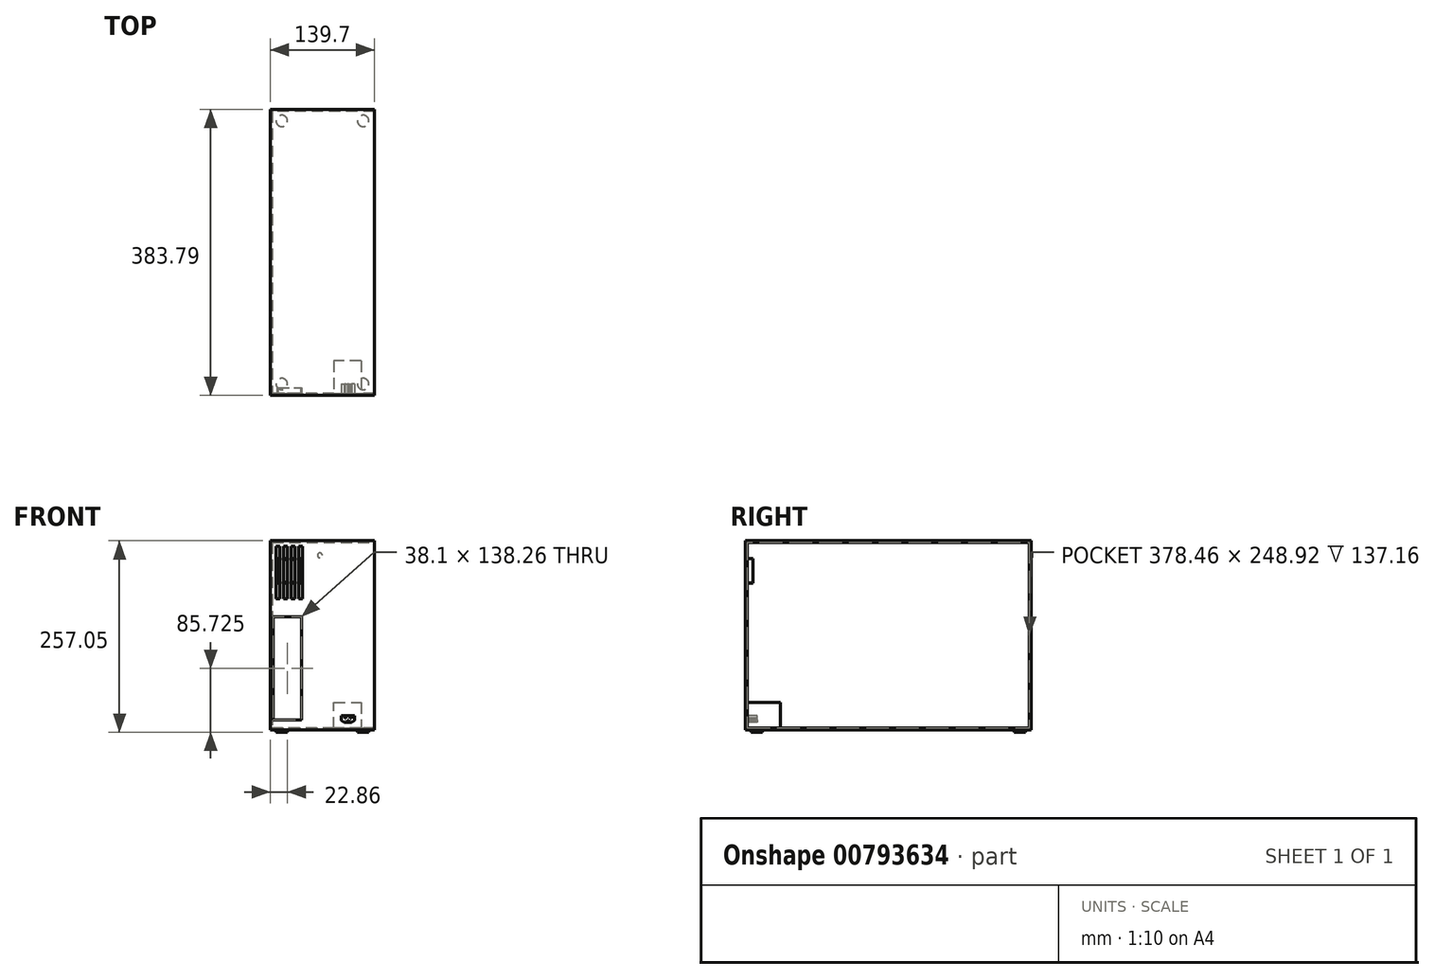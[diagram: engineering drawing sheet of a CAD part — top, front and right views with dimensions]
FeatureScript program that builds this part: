
annotation { "Feature Type Name" : "Feature", "Feature Type Description" : "" }
export const myFeature = defineFeature(function(context is Context, id is Id, definition is map)
    precondition{}
    {
        {
            var Q0;
            Q0=qCreatedBy(makeId("Top.planeOp"),FACE);
            var sketch = newSketch(context, id + "F0", { "sketchPlane" : qUnion([Q0])});
            skLineSegment(sketch, "E0", {"start": v(0, 0) * mm, "end": v(0, 381) * mm});
            skLineSegment(sketch, "E1", {"start": v(0, 381) * mm, "end": v(139.7, 381) * mm});
            skLineSegment(sketch, "E2", {"start": v(139.7, 381) * mm, "end": v(139.7, 0) * mm});
            skLineSegment(sketch, "E3", {"start": v(139.7, 0) * mm, "end": v(0, 0) * mm});
            skSolve(sketch);
        }
        {
            var Q0;
            Q0 = qSketchRegion(id + "F0", true);
            extrude(context, id + "F1", {"entities" : qUnion([Q0]), "depth" : 2.54 * mm, "offsetDistance" : 25.4 * mm});
        }
        {
            var Q0;
            Q0=qCreatedBy(makeId("Front.planeOp"),FACE);
            var sketch = newSketch(context, id + "F2", { "sketchPlane" : qUnion([Q0])});
            skLineSegment(sketch, "E4", {"start": v(0, 0) * mm, "end": v(0, 254) * mm});
            skLineSegment(sketch, "E5", {"start": v(0, 254) * mm, "end": v(139.7, 254) * mm});
            skLineSegment(sketch, "E6", {"start": v(139.7, 254) * mm, "end": v(139.7, 0) * mm});
            skLineSegment(sketch, "E7", {"start": v(139.7, 0) * mm, "end": v(0, 0) * mm});
            skSolve(sketch);
        }
        {
            var Q0;
            Q0 = qSketchRegion(id + "F2", true);
            extrude(context, id + "F3", {"entities" : qUnion([Q0]), "operationType" : NewBodyOperationType.ADD, "depth" : 2.54 * mm, "offsetDistance" : 25.4 * mm});
        }
        {
            var Q0;
            Q0=qCreatedBy(makeId("Right.planeOp"),FACE);
            var sketch = newSketch(context, id + "F4", { "sketchPlane" : qUnion([Q0])});
            skLineSegment(sketch, "E8", {"start": v(0, 0) * mm, "end": v(381, 0) * mm});
            skLineSegment(sketch, "E9", {"start": v(381, 0) * mm, "end": v(381, 254) * mm});
            skLineSegment(sketch, "E10", {"start": v(381, 254) * mm, "end": v(0, 254) * mm});
            skLineSegment(sketch, "E11", {"start": v(0, 254) * mm, "end": v(0, 0) * mm});
            skSolve(sketch);
        }
        {
            var Q0;
            Q0 = qSketchRegion(id + "F4", true);
            extrude(context, id + "F5", {"entities" : qUnion([Q0]), "operationType" : NewBodyOperationType.ADD, "depth" : 2.54 * mm, "offsetDistance" : 25.4 * mm});
        }
        {
            var Q0;
            Q0=qCreatedBy(makeId("Front.planeOp"),FACE);
            cPlane(context, id + "F6", {"entities" : qUnion([Q0]), "cplaneType" : CPlaneType.OFFSET, "offset" : 381 * mm, "oppositeDirection" : true, "width" : 152.4 * mm, "height" : 152.4 * mm});
        }
        {
            var Q0;
            Q0=qCreatedBy(id+"F6.planeOp",FACE);
            var sketch = newSketch(context, id + "F7", { "sketchPlane" : qUnion([Q0])});
            skLineSegment(sketch, "E12", {"start": v(0, 0) * mm, "end": v(0, 254) * mm});
            skLineSegment(sketch, "E13", {"start": v(0, 254) * mm, "end": v(139.7, 254) * mm});
            skLineSegment(sketch, "E14", {"start": v(139.7, 254) * mm, "end": v(139.7, 0) * mm});
            skLineSegment(sketch, "E15", {"start": v(139.7, 0) * mm, "end": v(0, 0) * mm});
            skSolve(sketch);
        }
        {
            var Q0;
            Q0 = qSketchRegion(id + "F7", true);
            extrude(context, id + "F8", {"entities" : qUnion([Q0]), "operationType" : NewBodyOperationType.ADD, "depth" : 2.54 * mm, "offsetDistance" : 25.4 * mm});
        }
        {
            var Q0;
            Q0=qCreatedBy(makeId("Top.planeOp"),FACE);
            cPlane(context, id + "F9", {"entities" : qUnion([Q0]), "cplaneType" : CPlaneType.OFFSET, "offset" : 254 * mm, "width" : 152.4 * mm, "height" : 152.4 * mm});
        }
        {
            var Q0;
            Q0=qCreatedBy(id+"F9.planeOp",FACE);
            var sketch = newSketch(context, id + "F10", { "sketchPlane" : qUnion([Q0])});
            skLineSegment(sketch, "E16", {"start": v(0, 0) * mm, "end": v(139.7, 0) * mm});
            skLineSegment(sketch, "E17", {"start": v(139.7, 0) * mm, "end": v(139.7, 381) * mm});
            skLineSegment(sketch, "E18", {"start": v(139.7, 381) * mm, "end": v(0, 381) * mm});
            skLineSegment(sketch, "E19", {"start": v(0, 381) * mm, "end": v(0, 0) * mm});
            skSolve(sketch);
        }
        {
            var Q0;
            Q0 = qSketchRegion(id + "F10", true);
            extrude(context, id + "F11", {"entities" : qUnion([Q0]), "operationType" : NewBodyOperationType.ADD, "oppositeDirection" : true, "depth" : 2.54 * mm, "offsetDistance" : 25.4 * mm});
        }
        {
            var Q0;
            Q0=makeQuery(id+"F3.opExtrude","CAP_FACE",FACE,{"disambiguationData":[OSD([sQuery(id+"F2.wireOp",EDGE,"E4"),sQuery(id+"F2.wireOp",EDGE,"E5"),sQuery(id+"F2.wireOp",EDGE,"E6"),sQuery(id+"F2.wireOp",EDGE,"E7")])],"isStart":false});
            var sketch = newSketch(context, id + "F12", { "sketchPlane" : qUnion([Q0])});
            skLineSegment(sketch, "E20", {"start": v(7.62, 175.93) * mm, "end": v(7.62, 246.38) * mm});
            skLineSegment(sketch, "E21", {"start": v(7.62, 246.38) * mm, "end": v(12.7, 246.38) * mm});
            skLineSegment(sketch, "E22", {"start": v(12.7, 246.38) * mm, "end": v(12.7, 175.93) * mm});
            skLineSegment(sketch, "E23", {"start": v(12.7, 7.62) * mm, "end": v(7.62, 7.62) * mm});
            skLineSegment(sketch, "E24", {"start": v(17.78, 246.38) * mm, "end": v(17.78, 175.93) * mm});
            skLineSegment(sketch, "E25", {"start": v(17.78, 7.62) * mm, "end": v(22.86, 7.62) * mm});
            skLineSegment(sketch, "E26", {"start": v(22.86, 175.93) * mm, "end": v(22.86, 246.38) * mm});
            skLineSegment(sketch, "E27", {"start": v(22.86, 246.38) * mm, "end": v(17.78, 246.38) * mm});
            skLineSegment(sketch, "E28", {"start": v(27.94, 246.38) * mm, "end": v(27.94, 175.93) * mm});
            skLineSegment(sketch, "E29", {"start": v(27.94, 7.62) * mm, "end": v(33.02, 7.62) * mm});
            skLineSegment(sketch, "E30", {"start": v(33.02, 175.93) * mm, "end": v(33.02, 246.38) * mm});
            skLineSegment(sketch, "E31", {"start": v(33.02, 246.38) * mm, "end": v(27.94, 246.38) * mm});
            skLineSegment(sketch, "E32", {"start": v(38.1, 246.38) * mm, "end": v(38.1, 175.93) * mm});
            skLineSegment(sketch, "E33", {"start": v(38.1, 7.62) * mm, "end": v(43.18, 7.62) * mm});
            skLineSegment(sketch, "E34", {"start": v(43.18, 175.93) * mm, "end": v(43.18, 246.38) * mm});
            skLineSegment(sketch, "E35", {"start": v(43.18, 246.38) * mm, "end": v(38.1, 246.38) * mm});
            skLineSegment(sketch, "E36", {"start": v(7.62, 175.93) * mm, "end": v(12.7, 175.93) * mm});
            skLineSegment(sketch, "E37.trimOffspring", {"start": v(17.78, 175.93) * mm, "end": v(22.86, 175.93) * mm});
            skLineSegment(sketch, "E38.trimOffspring", {"start": v(27.94, 175.93) * mm, "end": v(33.02, 175.93) * mm});
            skLineSegment(sketch, "E39.trimOffspring", {"start": v(38.1, 175.93) * mm, "end": v(43.18, 175.93) * mm});
            skSolve(sketch);
        }
        {
            var Q0;
            Q0=makeQuery(id+"F12.imprint","IMPRINT",FACE,{"disambiguationData":[TD([[makeQuery(id+"F12.imprint","IMPRINT",EDGE,{"derivedFrom":sQuery(id+"F12.wireOp",EDGE,"E32")}),1.0]])]});
            var Q1;
            Q1=makeQuery(id+"F12.imprint","IMPRINT",FACE,{"disambiguationData":[TD([[makeQuery(id+"F12.imprint","IMPRINT",EDGE,{"derivedFrom":sQuery(id+"F12.wireOp",EDGE,"E28")}),1.0]])]});
            var Q2;
            Q2=makeQuery(id+"F12.imprint","IMPRINT",FACE,{"disambiguationData":[TD([[makeQuery(id+"F12.imprint","IMPRINT",EDGE,{"derivedFrom":sQuery(id+"F12.wireOp",EDGE,"E24")}),1.0]])]});
            var Q3;
            Q3=makeQuery(id+"F12.imprint","IMPRINT",FACE,{"disambiguationData":[TD([[makeQuery(id+"F12.imprint","IMPRINT",EDGE,{"derivedFrom":sQuery(id+"F12.wireOp",EDGE,"E20")}),-1.0]])]});
            extrude(context, id + "F13", {"entities" : qUnion([Q0, Q1, Q2, Q3]), "operationType" : NewBodyOperationType.REMOVE, "oppositeDirection" : true, "depth" : 2.54 * mm, "offsetDistance" : 25.4 * mm});
        }
        {
            var Q0;
            Q0=qCreatedBy(makeId("Front.planeOp"),FACE);
            var sketch = newSketch(context, id + "F14", { "sketchPlane" : qUnion([Q0])});
            skLineSegment(sketch, "E40", {"start": v(0, 0) * mm, "end": v(0, 238.76) * mm});
            skLineSegment(sketch, "E41", {"start": v(40.69, 228.6) * mm, "end": v(40.69, 198.12) * mm});
            skLineSegment(sketch, "E42", {"start": v(10.21, 198.12) * mm, "end": v(10.21, 228.6) * mm});
            skLineSegment(sketch, "E43", {"start": v(40.69, 198.12) * mm, "end": v(40.69, 228.6) * mm});
            skLineSegment(sketch, "E44", {"start": v(40.69, 228.6) * mm, "end": v(10.21, 228.6) * mm});
            skLineSegment(sketch, "E45", {"start": v(10.21, 228.6) * mm, "end": v(10.21, 198.12) * mm});
            skLineSegment(sketch, "E46", {"start": v(10.21, 198.12) * mm, "end": v(40.69, 198.12) * mm});
            skLineSegment(sketch, "E47", {"start": v(8.94, 229.87) * mm, "end": v(41.96, 229.87) * mm});
            skLineSegment(sketch, "E48", {"start": v(41.96, 229.87) * mm, "end": v(41.96, 196.85) * mm});
            skLineSegment(sketch, "E49", {"start": v(41.96, 196.85) * mm, "end": v(8.94, 196.85) * mm});
            skLineSegment(sketch, "E50", {"start": v(8.94, 229.87) * mm, "end": v(8.94, 196.85) * mm});
            skLineSegment(sketch, "E51", {"start": v(10.21, 198.12) * mm, "end": v(25.45, 198.12) * mm});
            skLineSegment(sketch, "E52", {"start": v(25.45, 198.12) * mm, "end": v(25.45, 213.36) * mm});
            skSolve(sketch);
        }
        {
            var Q0;
            {var subQ3=sQuery(id+"F14.wireOp",EDGE,"E41");Q0=makeQuery(id+"F14.imprint","IMPRINT",FACE,{"disambiguationData":[TD([[makeQuery(id+"F14.imprint","IMPRINT",EDGE,{"derivedFrom":subQ3}),1.0]])]});}
            extrude(context, id + "F15", {"entities" : qUnion([Q0]), "operationType" : NewBodyOperationType.ADD, "oppositeDirection" : true, "depth" : 7.62 * mm, "offsetDistance" : 25.4 * mm});
        }
        {
            var Q0;
            Q0=qCreatedBy(makeId("Right.planeOp"),FACE);
            cPlane(context, id + "F16", {"entities" : qUnion([Q0]), "cplaneType" : CPlaneType.OFFSET, "offset" : 139.7 * mm, "width" : 152.4 * mm, "height" : 152.4 * mm});
        }
        {
            var Q0;
            Q0=qCreatedBy(id+"F16.planeOp",FACE);
            var sketch = newSketch(context, id + "F17", { "sketchPlane" : qUnion([Q0])});
            skCircle(sketch, "E53", {"center": v(187.96, 127) * mm, "radius": 120.65 * mm});
            skPoint(sketch, "E54.orphan", {"position": v(0, 0) * mm});
            skArc(sketch, "E55", {"start": v(194.31, 19.24) * mm, "mid": v(264.3, 50.67) * mm, "end": v(295.72, 120.65) * mm});
            skArc(sketch, "E56", {"start": v(194.3, 31.96) * mm, "mid": v(255.31, 59.65) * mm, "end": v(283, 120.65) * mm});
            skArc(sketch, "E57", {"start": v(194.31, 44.7) * mm, "mid": v(246.33, 68.63) * mm, "end": v(270.27, 120.65) * mm});
            skArc(sketch, "E58", {"start": v(194.3, 57.44) * mm, "mid": v(237.35, 77.6) * mm, "end": v(257.52, 120.65) * mm});
            skArc(sketch, "E59", {"start": v(194.3, 70.2) * mm, "mid": v(228.37, 86.59) * mm, "end": v(244.76, 120.65) * mm});
            skArc(sketch, "E60", {"start": v(194.3, 83) * mm, "mid": v(219.4, 95.57) * mm, "end": v(231.95, 120.65) * mm});
            skArc(sketch, "E61", {"start": v(194.31, 95.9) * mm, "mid": v(210.41, 104.55) * mm, "end": v(219.07, 120.65) * mm});
            skArc(sketch, "E62", {"start": v(194.3, 109.04) * mm, "mid": v(201.43, 113.53) * mm, "end": v(205.92, 120.65) * mm});
            skLineSegment(sketch, "E63", {"start": v(187.96, 133.35) * mm, "end": v(67.48, 133.35) * mm});
            skLineSegment(sketch, "E64", {"start": v(187.96, 120.65) * mm, "end": v(67.48, 120.65) * mm});
            skLineSegment(sketch, "E65", {"start": v(187.96, 120.65) * mm, "end": v(308.44, 120.65) * mm});
            skLineSegment(sketch, "E66", {"start": v(187.96, 133.35) * mm, "end": v(308.44, 133.35) * mm});
            skLineSegment(sketch, "E67", {"start": v(194.3, 127) * mm, "end": v(194.3, 247.48) * mm});
            skLineSegment(sketch, "E68", {"start": v(181.61, 127) * mm, "end": v(181.61, 247.48) * mm});
            skLineSegment(sketch, "E69", {"start": v(194.3, 127) * mm, "end": v(194.3, 6.52) * mm});
            skLineSegment(sketch, "E70", {"start": v(181.61, 127) * mm, "end": v(181.61, 6.52) * mm});
            skArc(sketch, "E71.trimOffspring", {"start": v(205.92, 133.35) * mm, "mid": v(201.43, 140.47) * mm, "end": v(194.3, 144.96) * mm});
            skArc(sketch, "E72.trimOffspring", {"start": v(219.07, 133.35) * mm, "mid": v(210.41, 149.45) * mm, "end": v(194.3, 158.1) * mm});
            skArc(sketch, "E73.trimOffspring", {"start": v(231.95, 133.35) * mm, "mid": v(219.4, 158.43) * mm, "end": v(194.3, 171) * mm});
            skArc(sketch, "E74.trimOffspring", {"start": v(244.76, 133.35) * mm, "mid": v(228.37, 167.41) * mm, "end": v(194.3, 183.8) * mm});
            skArc(sketch, "E75.trimOffspring", {"start": v(257.52, 133.35) * mm, "mid": v(237.35, 176.4) * mm, "end": v(194.3, 196.56) * mm});
            skArc(sketch, "E76.trimOffspring", {"start": v(270.27, 133.35) * mm, "mid": v(246.33, 185.37) * mm, "end": v(194.3, 209.3) * mm});
            skArc(sketch, "E77.trimOffspring", {"start": v(283, 133.35) * mm, "mid": v(255.31, 194.35) * mm, "end": v(194.3, 222.04) * mm});
            skArc(sketch, "E78.trimOffspring", {"start": v(295.72, 133.35) * mm, "mid": v(264.3, 203.33) * mm, "end": v(194.3, 234.76) * mm});
            skArc(sketch, "E79.trimOffspring", {"start": v(170, 120.65) * mm, "mid": v(174.49, 113.53) * mm, "end": v(181.61, 109.04) * mm});
            skArc(sketch, "E80.trimOffspring", {"start": v(156.85, 120.65) * mm, "mid": v(165.5, 104.55) * mm, "end": v(181.6, 95.9) * mm});
            skArc(sketch, "E81.trimOffspring", {"start": v(143.97, 120.65) * mm, "mid": v(156.53, 95.57) * mm, "end": v(181.6, 83) * mm});
            skArc(sketch, "E82.trimOffspring", {"start": v(131.16, 120.65) * mm, "mid": v(147.55, 86.59) * mm, "end": v(181.61, 70.2) * mm});
            skArc(sketch, "E83.trimOffspring", {"start": v(118.4, 120.65) * mm, "mid": v(138.57, 77.6) * mm, "end": v(181.61, 57.44) * mm});
            skArc(sketch, "E84.trimOffspring", {"start": v(105.65, 120.65) * mm, "mid": v(129.59, 68.63) * mm, "end": v(181.6, 44.7) * mm});
            skArc(sketch, "E85.trimOffspring", {"start": v(92.92, 120.65) * mm, "mid": v(120.6, 59.65) * mm, "end": v(181.61, 31.96) * mm});
            skArc(sketch, "E86.trimOffspring", {"start": v(80.2, 120.65) * mm, "mid": v(111.63, 50.67) * mm, "end": v(181.6, 19.24) * mm});
            skArc(sketch, "E87.trimOffspring", {"start": v(181.61, 234.76) * mm, "mid": v(111.63, 203.33) * mm, "end": v(80.2, 133.35) * mm});
            skArc(sketch, "E88.trimOffspring", {"start": v(181.61, 222.04) * mm, "mid": v(120.6, 194.35) * mm, "end": v(92.92, 133.35) * mm});
            skArc(sketch, "E89.trimOffspring", {"start": v(181.61, 209.3) * mm, "mid": v(129.59, 185.37) * mm, "end": v(105.65, 133.35) * mm});
            skArc(sketch, "E90.trimOffspring", {"start": v(181.61, 196.56) * mm, "mid": v(138.57, 176.4) * mm, "end": v(118.4, 133.35) * mm});
            skArc(sketch, "E91.trimOffspring", {"start": v(181.61, 183.8) * mm, "mid": v(147.55, 167.41) * mm, "end": v(131.16, 133.35) * mm});
            skArc(sketch, "E92.trimOffspring", {"start": v(181.61, 171) * mm, "mid": v(156.53, 158.43) * mm, "end": v(143.97, 133.35) * mm});
            skArc(sketch, "E93.trimOffspring", {"start": v(181.61, 158.1) * mm, "mid": v(165.5, 149.45) * mm, "end": v(156.85, 133.35) * mm});
            skArc(sketch, "E94.trimOffspring", {"start": v(181.61, 144.96) * mm, "mid": v(174.49, 140.47) * mm, "end": v(170, 133.35) * mm});
            skSolve(sketch);
        }
        {
            var Q0;
            {var subQ5=sQuery(id+"F17.wireOp",EDGE,"E87.trimOffspring");Q0=makeQuery(id+"F17.imprint","IMPRINT",FACE,{"disambiguationData":[TD([[makeQuery(id+"F17.imprint","IMPRINT",EDGE,{"derivedFrom":subQ5}),-1.0]])]});}
            var Q1;
            {var subQ0=sQuery(id+"F17.wireOp",EDGE,"E88.trimOffspring");Q1=makeQuery(id+"F17.imprint","IMPRINT",FACE,{"disambiguationData":[TD([[makeQuery(id+"F17.imprint","IMPRINT",EDGE,{"derivedFrom":subQ0}),1.0]])]});}
            var Q2;
            {var subQ0=sQuery(id+"F17.wireOp",EDGE,"E90.trimOffspring");Q2=makeQuery(id+"F17.imprint","IMPRINT",FACE,{"disambiguationData":[TD([[makeQuery(id+"F17.imprint","IMPRINT",EDGE,{"derivedFrom":subQ0}),1.0]])]});}
            var Q3;
            {var subQ0=sQuery(id+"F17.wireOp",EDGE,"E92.trimOffspring");Q3=makeQuery(id+"F17.imprint","IMPRINT",FACE,{"disambiguationData":[TD([[makeQuery(id+"F17.imprint","IMPRINT",EDGE,{"derivedFrom":subQ0}),1.0]])]});}
            var Q4;
            {var subQ0=sQuery(id+"F17.wireOp",EDGE,"E94.trimOffspring");Q4=makeQuery(id+"F17.imprint","IMPRINT",FACE,{"disambiguationData":[TD([[makeQuery(id+"F17.imprint","IMPRINT",EDGE,{"derivedFrom":subQ0}),1.0]])]});}
            var Q5;
            {var subQ0=sQuery(id+"F17.wireOp",EDGE,"E71.trimOffspring");Q5=makeQuery(id+"F17.imprint","IMPRINT",FACE,{"disambiguationData":[TD([[makeQuery(id+"F17.imprint","IMPRINT",EDGE,{"derivedFrom":subQ0}),1.0]])]});}
            var Q6;
            {var subQ0=sQuery(id+"F17.wireOp",EDGE,"E72.trimOffspring");Q6=makeQuery(id+"F17.imprint","IMPRINT",FACE,{"disambiguationData":[TD([[makeQuery(id+"F17.imprint","IMPRINT",EDGE,{"derivedFrom":subQ0}),-1.0]])]});}
            var Q7;
            {var subQ0=sQuery(id+"F17.wireOp",EDGE,"E74.trimOffspring");Q7=makeQuery(id+"F17.imprint","IMPRINT",FACE,{"disambiguationData":[TD([[makeQuery(id+"F17.imprint","IMPRINT",EDGE,{"derivedFrom":subQ0}),-1.0]])]});}
            var Q8;
            {var subQ0=sQuery(id+"F17.wireOp",EDGE,"E76.trimOffspring");Q8=makeQuery(id+"F17.imprint","IMPRINT",FACE,{"disambiguationData":[TD([[makeQuery(id+"F17.imprint","IMPRINT",EDGE,{"derivedFrom":subQ0}),-1.0]])]});}
            var Q9;
            {var subQ5=sQuery(id+"F17.wireOp",EDGE,"E78.trimOffspring");Q9=makeQuery(id+"F17.imprint","IMPRINT",FACE,{"disambiguationData":[TD([[makeQuery(id+"F17.imprint","IMPRINT",EDGE,{"derivedFrom":subQ5}),-1.0]])]});}
            var Q10;
            {var subQ5=sQuery(id+"F17.wireOp",EDGE,"E55");Q10=makeQuery(id+"F17.imprint","IMPRINT",FACE,{"disambiguationData":[TD([[makeQuery(id+"F17.imprint","IMPRINT",EDGE,{"derivedFrom":subQ5}),-1.0]])]});}
            var Q11;
            {var subQ0=sQuery(id+"F17.wireOp",EDGE,"E56");Q11=makeQuery(id+"F17.imprint","IMPRINT",FACE,{"disambiguationData":[TD([[makeQuery(id+"F17.imprint","IMPRINT",EDGE,{"derivedFrom":subQ0}),1.0]])]});}
            var Q12;
            {var subQ0=sQuery(id+"F17.wireOp",EDGE,"E58");Q12=makeQuery(id+"F17.imprint","IMPRINT",FACE,{"disambiguationData":[TD([[makeQuery(id+"F17.imprint","IMPRINT",EDGE,{"derivedFrom":subQ0}),1.0]])]});}
            var Q13;
            {var subQ0=sQuery(id+"F17.wireOp",EDGE,"E60");Q13=makeQuery(id+"F17.imprint","IMPRINT",FACE,{"disambiguationData":[TD([[makeQuery(id+"F17.imprint","IMPRINT",EDGE,{"derivedFrom":subQ0}),1.0]])]});}
            var Q14;
            {var subQ0=sQuery(id+"F17.wireOp",EDGE,"E62");Q14=makeQuery(id+"F17.imprint","IMPRINT",FACE,{"disambiguationData":[TD([[makeQuery(id+"F17.imprint","IMPRINT",EDGE,{"derivedFrom":subQ0}),1.0]])]});}
            var Q15;
            {var subQ5=sQuery(id+"F17.wireOp",EDGE,"E86.trimOffspring");Q15=makeQuery(id+"F17.imprint","IMPRINT",FACE,{"disambiguationData":[TD([[makeQuery(id+"F17.imprint","IMPRINT",EDGE,{"derivedFrom":subQ5}),-1.0]])]});}
            var Q16;
            {var subQ0=sQuery(id+"F17.wireOp",EDGE,"E84.trimOffspring");Q16=makeQuery(id+"F17.imprint","IMPRINT",FACE,{"disambiguationData":[TD([[makeQuery(id+"F17.imprint","IMPRINT",EDGE,{"derivedFrom":subQ0}),-1.0]])]});}
            var Q17;
            {var subQ0=sQuery(id+"F17.wireOp",EDGE,"E82.trimOffspring");Q17=makeQuery(id+"F17.imprint","IMPRINT",FACE,{"disambiguationData":[TD([[makeQuery(id+"F17.imprint","IMPRINT",EDGE,{"derivedFrom":subQ0}),-1.0]])]});}
            var Q18;
            {var subQ0=sQuery(id+"F17.wireOp",EDGE,"E80.trimOffspring");Q18=makeQuery(id+"F17.imprint","IMPRINT",FACE,{"disambiguationData":[TD([[makeQuery(id+"F17.imprint","IMPRINT",EDGE,{"derivedFrom":subQ0}),-1.0]])]});}
            var Q19;
            {var subQ0=sQuery(id+"F17.wireOp",EDGE,"E79.trimOffspring");Q19=makeQuery(id+"F17.imprint","IMPRINT",FACE,{"disambiguationData":[TD([[makeQuery(id+"F17.imprint","IMPRINT",EDGE,{"derivedFrom":subQ0}),1.0]])]});}
            extrude(context, id + "F18", {"entities" : qUnion([Q0, Q1, Q2, Q3, Q4, Q5, Q6, Q7, Q8, Q9, Q10, Q11, Q12, Q13, Q14, Q15, Q16, Q17, Q18, Q19]), "operationType" : NewBodyOperationType.REMOVE, "oppositeDirection" : true, "depth" : 2.54 * mm, "offsetDistance" : 25.4 * mm});
        }
        {
            var Q0;
            Q0=makeQuery(id+"F8.boolean.opBoolean","MERGE",FACE,{"derivedFrom":[makeQuery(id+"F5.boolean.opBoolean","MERGE",FACE,{"derivedFrom":[makeQuery(id+"F1.opExtrude","SWEPT_FACE",FACE,{"disambiguationData":[OSD([sQuery(id+"F0.wireOp",EDGE,"E1")])]}),makeQuery(id+"F5.opExtrude","SWEPT_FACE",FACE,{"disambiguationData":[OSD([sQuery(id+"F4.wireOp",EDGE,"E9")])]})]}),makeQuery(id+"F8.opExtrude","CAP_FACE",FACE,{"disambiguationData":[OSD([sQuery(id+"F7.wireOp",EDGE,"E12"),sQuery(id+"F7.wireOp",EDGE,"E13"),sQuery(id+"F7.wireOp",EDGE,"E14"),sQuery(id+"F7.wireOp",EDGE,"E15")])],"isStart":true})]});
            var sketch = newSketch(context, id + "F19", { "sketchPlane" : qUnion([Q0])});
            skCircle(sketch, "E95", {"center": v(-66.47, 234.4) * mm, "radius": 3.18 * mm});
            skSolve(sketch);
        }
        {
            var Q0;
            Q0=makeQuery(id+"F19.imprint","IMPRINT",FACE,{"disambiguationData":[TD([[makeQuery(id+"F19.imprint","IMPRINT",EDGE,{"derivedFrom":sQuery(id+"F19.wireOp",EDGE,"E95")}),1.0]])]});
            extrude(context, id + "F20", {"entities" : qUnion([Q0]), "operationType" : NewBodyOperationType.ADD, "depth" : 0.25 * mm, "offsetDistance" : 25.4 * mm});
        }
        {
            var Q0;
            Q0=makeQuery(id+"F3.opExtrude","CAP_FACE",FACE,{"disambiguationData":[OSD([sQuery(id+"F2.wireOp",EDGE,"E4"),sQuery(id+"F2.wireOp",EDGE,"E5"),sQuery(id+"F2.wireOp",EDGE,"E6"),sQuery(id+"F2.wireOp",EDGE,"E7")])],"isStart":false});
            var sketch = newSketch(context, id + "F21", { "sketchPlane" : qUnion([Q0])});
            skLineSegment(sketch, "E96", {"start": v(95.25, 12.7) * mm, "end": v(95.25, 19.05) * mm});
            skLineSegment(sketch, "E97", {"start": v(95.25, 19.05) * mm, "end": v(113.03, 19.05) * mm});
            skLineSegment(sketch, "E98", {"start": v(113.03, 19.05) * mm, "end": v(113.03, 12.7) * mm});
            skLineSegment(sketch, "E99", {"start": v(113.03, 12.7) * mm, "end": v(109.38, 10.6) * mm});
            skLineSegment(sketch, "E100", {"start": v(95.25, 12.7) * mm, "end": v(98.9, 10.6) * mm});
            skLineSegment(sketch, "E101", {"start": v(98.9, 10.6) * mm, "end": v(109.38, 10.6) * mm});
            skPoint(sketch, "E102.start.orphan", {"position": v(69.85, 0) * mm});
            skSolve(sketch);
        }
        {
            var Q0;
            Q0=makeQuery(id+"F21.imprint","IMPRINT",FACE,{"disambiguationData":[TD([[makeQuery(id+"F21.imprint","IMPRINT",EDGE,{"derivedFrom":sQuery(id+"F21.wireOp",EDGE,"E96")}),-1.0]])]});
            extrude(context, id + "F22", {"entities" : qUnion([Q0]), "operationType" : NewBodyOperationType.REMOVE, "oppositeDirection" : true, "depth" : 2.54 * mm, "offsetDistance" : 25.4 * mm});
        }
        {
            var Q0;
            Q0=makeQuery(id+"F3.boolean.opBoolean","MERGE",FACE,{"derivedFrom":[makeQuery(id+"F1.opExtrude","CAP_FACE",FACE,{"disambiguationData":[OSD([sQuery(id+"F0.wireOp",EDGE,"E0"),sQuery(id+"F0.wireOp",EDGE,"E1"),sQuery(id+"F0.wireOp",EDGE,"E2"),sQuery(id+"F0.wireOp",EDGE,"E3")])],"isStart":true}),makeQuery(id+"F3.opExtrude","SWEPT_FACE",FACE,{"disambiguationData":[OSD([sQuery(id+"F2.wireOp",EDGE,"E7")])]})]});
            var sketch = newSketch(context, id + "F23", { "sketchPlane" : qUnion([Q0])});
            skLineSegment(sketch, "E103", {"start": v(0, 2.54) * mm, "end": v(15.24, 2.54) * mm});
            skLineSegment(sketch, "E104", {"start": v(15.24, 2.54) * mm, "end": v(15.24, -12.7) * mm});
            skCircle(sketch, "E105", {"center": v(15.24, -12.7) * mm, "radius": 7.62 * mm});
            skLineSegment(sketch, "E106", {"start": v(139.7, 2.54) * mm, "end": v(124.46, 2.54) * mm});
            skLineSegment(sketch, "E107", {"start": v(124.46, 2.54) * mm, "end": v(124.46, -12.7) * mm});
            skCircle(sketch, "E108", {"center": v(124.46, -12.7) * mm, "radius": 7.62 * mm});
            skLineSegment(sketch, "E109", {"start": v(139.7, -381) * mm, "end": v(124.46, -381) * mm});
            skLineSegment(sketch, "E110", {"start": v(124.46, -381) * mm, "end": v(124.46, -365.76) * mm});
            skCircle(sketch, "E111", {"center": v(124.46, -365.76) * mm, "radius": 7.62 * mm});
            skLineSegment(sketch, "E112", {"start": v(0, -381) * mm, "end": v(15.24, -381) * mm});
            skLineSegment(sketch, "E113", {"start": v(15.24, -381) * mm, "end": v(15.24, -365.76) * mm});
            skCircle(sketch, "E114", {"center": v(15.24, -365.76) * mm, "radius": 7.62 * mm});
            skSolve(sketch);
        }
        {
            var Q0;
            Q0=makeQuery(id+"F23.imprint","IMPRINT",FACE,{"disambiguationData":[TD([[makeQuery(id+"F23.imprint","IMPRINT",EDGE,{"derivedFrom":sQuery(id+"F23.wireOp",EDGE,"E114")}),1.0]])]});
            var Q1;
            Q1=makeQuery(id+"F23.imprint","IMPRINT",FACE,{"disambiguationData":[TD([[makeQuery(id+"F23.imprint","IMPRINT",EDGE,{"derivedFrom":sQuery(id+"F23.wireOp",EDGE,"E111")}),1.0]])]});
            var Q2;
            Q2=makeQuery(id+"F23.imprint","IMPRINT",FACE,{"disambiguationData":[TD([[makeQuery(id+"F23.imprint","IMPRINT",EDGE,{"derivedFrom":sQuery(id+"F23.wireOp",EDGE,"E108")}),1.0]])]});
            var Q3;
            Q3=makeQuery(id+"F23.imprint","IMPRINT",FACE,{"disambiguationData":[TD([[makeQuery(id+"F23.imprint","IMPRINT",EDGE,{"derivedFrom":sQuery(id+"F23.wireOp",EDGE,"E105")}),1.0]])]});
            extrude(context, id + "F24", {"entities" : qUnion([Q0, Q1, Q2, Q3]), "operationType" : NewBodyOperationType.ADD, "depth" : 3.05 * mm, "offsetDistance" : 25.4 * mm});
        }
        {
            var Q0;
            Q0=makeQuery(id+"F3.opExtrude","CAP_FACE",FACE,{"disambiguationData":[OSD([sQuery(id+"F2.wireOp",EDGE,"E4"),sQuery(id+"F2.wireOp",EDGE,"E5"),sQuery(id+"F2.wireOp",EDGE,"E6"),sQuery(id+"F2.wireOp",EDGE,"E7")])],"isStart":false});
            var sketch = newSketch(context, id + "F25", { "sketchPlane" : qUnion([Q0])});
            skLineSegment(sketch, "E115", {"start": v(0, 151.8) * mm, "end": v(3.81, 151.8) * mm});
            skLineSegment(sketch, "E116", {"start": v(3.81, 151.8) * mm, "end": v(3.81, 13.54) * mm});
            skLineSegment(sketch, "E117", {"start": v(3.81, 13.54) * mm, "end": v(41.91, 13.54) * mm});
            skLineSegment(sketch, "E118", {"start": v(41.91, 13.54) * mm, "end": v(41.91, 151.8) * mm});
            skLineSegment(sketch, "E119", {"start": v(41.91, 151.8) * mm, "end": v(3.81, 151.8) * mm});
            skSolve(sketch);
        }
        {
            var Q0;
            Q0=makeQuery(id+"F25.imprint","IMPRINT",FACE,{"disambiguationData":[TD([[makeQuery(id+"F25.imprint","IMPRINT",EDGE,{"derivedFrom":sQuery(id+"F25.wireOp",EDGE,"E116")}),1.0]])]});
            extrude(context, id + "F26", {"entities" : qUnion([Q0]), "operationType" : NewBodyOperationType.REMOVE, "oppositeDirection" : true, "depth" : 2.54 * mm, "offsetDistance" : 25.4 * mm});
        }
        {
            var Q0;
            Q0=qCreatedBy(makeId("Front.planeOp"),FACE);
            var sketch = newSketch(context, id + "F27", { "sketchPlane" : qUnion([Q0])});
            skLineSegment(sketch, "E120", {"start": v(85.27, 0) * mm, "end": v(85.27, 2.54) * mm});
            skLineSegment(sketch, "E121", {"start": v(85.27, 2.54) * mm, "end": v(85.27, 37.04) * mm});
            skLineSegment(sketch, "E122", {"start": v(85.27, 37.04) * mm, "end": v(121.74, 37.04) * mm});
            skLineSegment(sketch, "E123", {"start": v(121.74, 37.04) * mm, "end": v(121.74, 2.54) * mm});
            skLineSegment(sketch, "E124", {"start": v(121.74, 2.54) * mm, "end": v(85.27, 2.54) * mm});
            skSolve(sketch);
        }
        {
            var Q0;
            Q0 = qSketchRegion(id + "F27", true);
            extrude(context, id + "F28", {"entities" : qUnion([Q0]), "operationType" : NewBodyOperationType.ADD, "oppositeDirection" : true, "depth" : 43.94 * mm, "offsetDistance" : 25.4 * mm});
        }
        {
            var Q0;
            Q0=makeQuery(id+"F28.opExtrude","CAP_FACE",FACE,{"disambiguationData":[OSD([sQuery(id+"F27.wireOp",EDGE,"E121"),sQuery(id+"F27.wireOp",EDGE,"E122"),sQuery(id+"F27.wireOp",EDGE,"E123"),sQuery(id+"F27.wireOp",EDGE,"E124")])],"isStart":true});
            var sketch = newSketch(context, id + "F29", { "sketchPlane" : qUnion([Q0])});
            skLineSegment(sketch, "E125", {"start": v(113.03, 19.05) * mm, "end": v(95.25, 19.05) * mm});
            skLineSegment(sketch, "E126", {"start": v(95.25, 19.05) * mm, "end": v(95.25, 12.7) * mm});
            skLineSegment(sketch, "E127", {"start": v(95.25, 12.7) * mm, "end": v(98.9, 10.6) * mm});
            skLineSegment(sketch, "E128", {"start": v(98.9, 10.6) * mm, "end": v(109.38, 10.6) * mm});
            skLineSegment(sketch, "E129", {"start": v(109.38, 10.6) * mm, "end": v(113.03, 12.7) * mm});
            skLineSegment(sketch, "E130", {"start": v(113.03, 12.7) * mm, "end": v(113.03, 19.05) * mm});
            skSolve(sketch);
        }
        {
            var Q0;
            Q0=makeQuery(id+"F29.imprint","IMPRINT",FACE,{"disambiguationData":[TD([[makeQuery(id+"F29.imprint","IMPRINT",EDGE,{"derivedFrom":sQuery(id+"F29.wireOp",EDGE,"E125")}),-1.0]])]});
            extrude(context, id + "F30", {"entities" : qUnion([Q0]), "operationType" : NewBodyOperationType.REMOVE, "oppositeDirection" : true, "depth" : 12.95 * mm, "offsetDistance" : 25.4 * mm});
        }
        {
            var Q0;
            Q0=makeQuery(id+"F30.boolean.opBoolean","COPY",FACE,{"derivedFrom":makeQuery(id+"F30.opExtrude","CAP_FACE",FACE,{"disambiguationData":[OSD([sQuery(id+"F29.wireOp",EDGE,"E125"),sQuery(id+"F29.wireOp",EDGE,"E126"),sQuery(id+"F29.wireOp",EDGE,"E127"),sQuery(id+"F29.wireOp",EDGE,"E128"),sQuery(id+"F29.wireOp",EDGE,"E129"),sQuery(id+"F29.wireOp",EDGE,"E130")])],"isStart":false})});
            var sketch = newSketch(context, id + "F31", { "sketchPlane" : qUnion([Q0])});
            skLineSegment(sketch, "E131", {"start": v(100.04, 16.76) * mm, "end": v(100.04, 15.33) * mm});
            skLineSegment(sketch, "E132", {"start": v(100.04, 15.33) * mm, "end": v(100.86, 15.33) * mm});
            skLineSegment(sketch, "E133", {"start": v(100.86, 15.33) * mm, "end": v(100.86, 16.76) * mm});
            skLineSegment(sketch, "E134", {"start": v(100.86, 16.76) * mm, "end": v(100.04, 16.76) * mm});
            skLineSegment(sketch, "E135", {"start": v(107.4, 15.33) * mm, "end": v(107.4, 16.76) * mm});
            skLineSegment(sketch, "E136", {"start": v(107.4, 16.76) * mm, "end": v(108.26, 16.76) * mm});
            skLineSegment(sketch, "E137", {"start": v(108.26, 16.76) * mm, "end": v(108.26, 15.33) * mm});
            skLineSegment(sketch, "E138", {"start": v(108.26, 15.33) * mm, "end": v(107.4, 15.33) * mm});
            skLineSegment(sketch, "E139", {"start": v(103.92, 13.65) * mm, "end": v(103.92, 12.63) * mm});
            skLineSegment(sketch, "E140", {"start": v(103.92, 12.63) * mm, "end": v(104.74, 12.63) * mm});
            skLineSegment(sketch, "E141", {"start": v(104.74, 12.63) * mm, "end": v(104.74, 13.65) * mm});
            skLineSegment(sketch, "E142", {"start": v(104.74, 13.65) * mm, "end": v(103.92, 13.65) * mm});
            skSolve(sketch);
        }
        {
            var Q0;
            Q0=makeQuery(id+"F31.imprint","IMPRINT",FACE,{"disambiguationData":[TD([[makeQuery(id+"F31.imprint","IMPRINT",EDGE,{"derivedFrom":sQuery(id+"F31.wireOp",EDGE,"E135")}),-1.0]])]});
            var Q1;
            Q1=makeQuery(id+"F31.imprint","IMPRINT",FACE,{"disambiguationData":[TD([[makeQuery(id+"F31.imprint","IMPRINT",EDGE,{"derivedFrom":sQuery(id+"F31.wireOp",EDGE,"E139")}),1.0]])]});
            var Q2;
            Q2=makeQuery(id+"F31.imprint","IMPRINT",FACE,{"disambiguationData":[TD([[makeQuery(id+"F31.imprint","IMPRINT",EDGE,{"derivedFrom":sQuery(id+"F31.wireOp",EDGE,"E131")}),1.0]])]});
            extrude(context, id + "F32", {"entities" : qUnion([Q0, Q1, Q2]), "operationType" : NewBodyOperationType.ADD, "depth" : 12.45 * mm, "offsetDistance" : 25.4 * mm});
        }
    });
